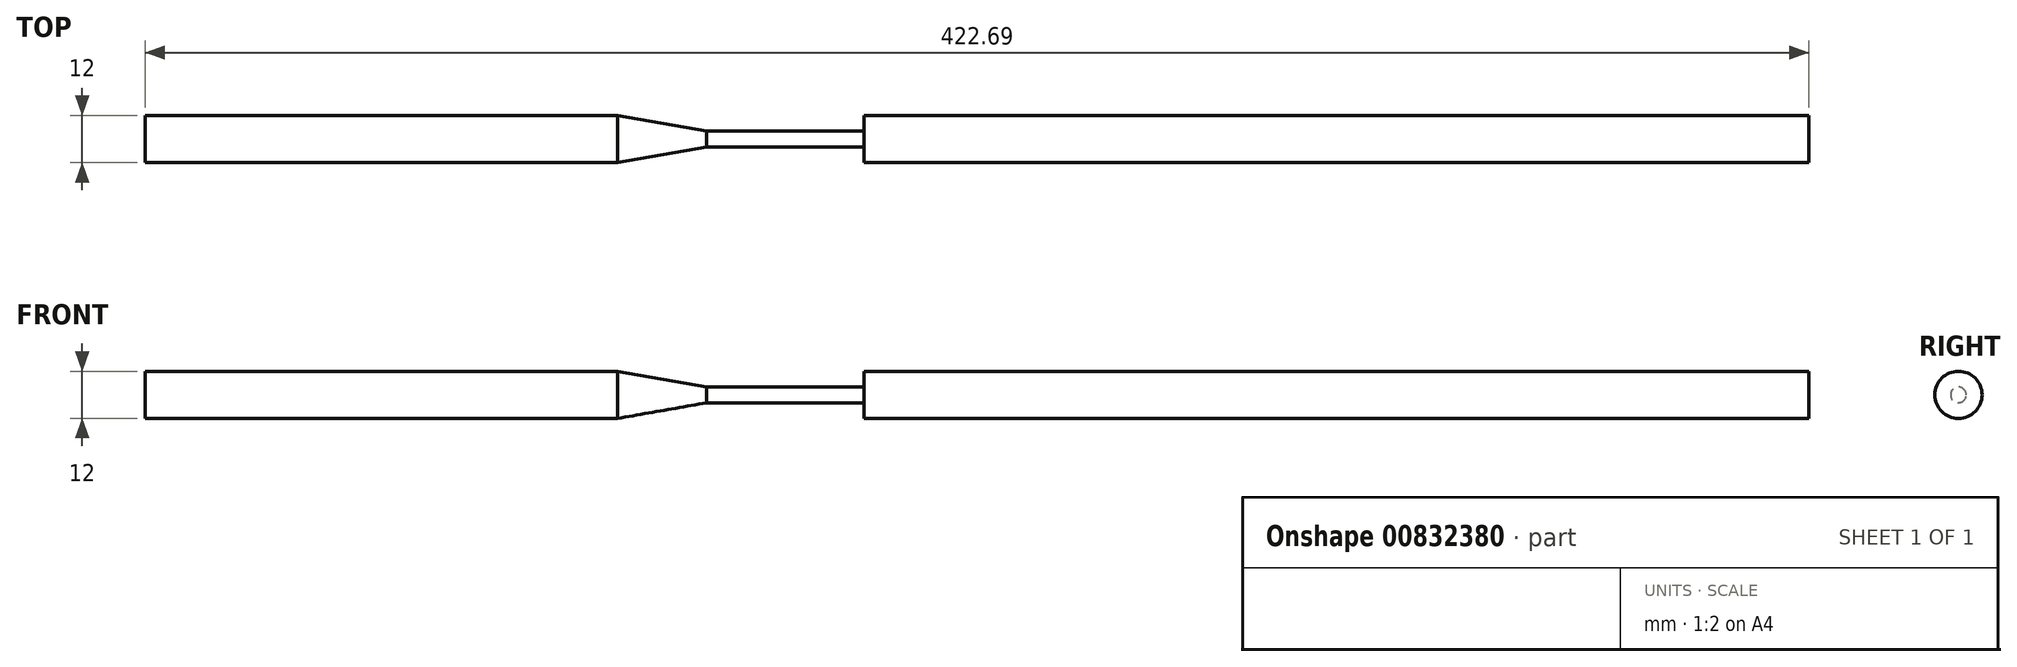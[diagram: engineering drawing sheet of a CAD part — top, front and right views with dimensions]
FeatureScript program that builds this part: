
annotation { "Feature Type Name" : "Feature", "Feature Type Description" : "" }
export const myFeature = defineFeature(function(context is Context, id is Id, definition is map)
    precondition{}
    {
        {
            var Q0;
            Q0=qCreatedBy(makeId("Right.planeOp"),FACE);
            var sketch = newSketch(context, id + "F0", { "sketchPlane" : qUnion([Q0])});
            skCircle(sketch, "E0", {"center": v(0, 0) * mm, "radius": 6 * mm});
            skSolve(sketch);
        }
        {
            var Q0;
            Q0 = qSketchRegion(id + "F0", true);
            extrude(context, id + "F1", {"entities" : qUnion([Q0]), "depth" : 120 * mm, "offsetDistance" : 25.4 * mm});
        }
        {
            var Q0;
            Q0=qCreatedBy(makeId("Right.planeOp"),FACE);
            cPlane(context, id + "F2", {"entities" : qUnion([Q0]), "cplaneType" : CPlaneType.OFFSET, "offset" : (142.69) * mm, "width" : 152.4 * mm, "height" : 152.4 * mm});
        }
        {
            var Q0;
            Q0=qCreatedBy(id+"F2.planeOp",FACE);
            var sketch = newSketch(context, id + "F3", { "sketchPlane" : qUnion([Q0])});
            skCircle(sketch, "E1", {"center": v(0, 0) * mm, "radius": 2 * mm});
            skSolve(sketch);
        }
        {
            var Q1;
            Q1=makeQuery(id+"F1.opExtrude","CAP_FACE",FACE,{"disambiguationData":[OSD([sQuery(id+"F0.wireOp",EDGE,"E0")])],"isStart":false});
            var Q2;
            Q2=makeQuery(id+"F3.imprint","IMPRINT",FACE,{"disambiguationData":[TD([[makeQuery(id+"F3.imprint","IMPRINT",EDGE,{"derivedFrom":sQuery(id+"F3.wireOp",EDGE,"E1")}),1.0]])]});
            loft(context, id + "F4", {"operationType" : NewBodyOperationType.ADD, "sheetProfilesArray" : [{ "sheetProfileEntities" : qUnion([Q1]) }, { "sheetProfileEntities" : qUnion([Q2]) }]});
        }
        {
            var Q0;
            Q0=qCreatedBy(id+"F2.planeOp",FACE);
            var sketch = newSketch(context, id + "F5", { "sketchPlane" : qUnion([Q0])});
            skCircle(sketch, "E2", {"center": v(0, 0) * mm, "radius": 2 * mm});
            skSolve(sketch);
        }
        {
            var Q0;
            Q0=makeQuery(id+"F5.imprint","IMPRINT",FACE,{"disambiguationData":[TD([[makeQuery(id+"F5.imprint","IMPRINT",EDGE,{"derivedFrom":sQuery(id+"F5.wireOp",EDGE,"E2")}),1.0]])]});
            extrude(context, id + "F6", {"entities" : qUnion([Q0]), "operationType" : NewBodyOperationType.ADD, "depth" : 40 * mm, "offsetDistance" : 25.4 * mm});
        }
        {
            var Q0;
            Q0=qCreatedBy(id+"F2.planeOp",FACE);
            cPlane(context, id + "F7", {"entities" : qUnion([Q0]), "cplaneType" : CPlaneType.OFFSET, "offset" : 40 * mm, "width" : 152.4 * mm, "height" : 152.4 * mm});
        }
        {
            var Q0;
            Q0=qCreatedBy(id+"F7.planeOp",FACE);
            var sketch = newSketch(context, id + "F8", { "sketchPlane" : qUnion([Q0])});
            skCircle(sketch, "E3", {"center": v(0, 0) * mm, "radius": 6 * mm});
            skSolve(sketch);
        }
        {
            var Q0;
            Q0 = qSketchRegion(id + "F8", true);
            extrude(context, id + "F9", {"entities" : qUnion([Q0]), "operationType" : NewBodyOperationType.ADD, "depth" : 240 * mm, "offsetDistance" : 25.4 * mm});
        }
    });
